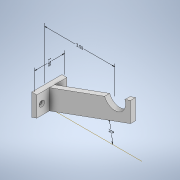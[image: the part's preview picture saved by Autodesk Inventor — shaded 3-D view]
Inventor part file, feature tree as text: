
AUTODESK INVENTOR PART (.ipt)
format: ipt  version: 2021.1 (Build 251245000, 245)  size: 155,136 bytes
history: native  units: in
note: dims shown in document units (in); Inventor stores cm internally (conversion verified against a paired STEP export)
features: other x4, sketch x4, extrude x3, hole x1
ambient origin geometry x8: Origin, YZ Plane, XZ Plane, XY Plane, X Axis, Y Axis, Z Axis, Center Point
bodies: Solid2 (feature_tree)
feature tree (12):
  other  "Annotations"
  extrude  "Extrusion3"  Depth=0.25in
  extrude  "Extrusion4"  Depth=1.5in
  sketch  "Sketch7"  dims[d26=1.075in d29=0.25in]
  extrude  "Extrusion5"  Depth=0.25in
  hole  "Hole3"  [1 undecoded]
  sketch  "Sketch5"  dims[d21=1.0in d22=0.25in]
  sketch  "Sketch6"  dims[d23=1.5in d24=0.0in d25=0.1374in]
  sketch  "Sketch8"  dims[d30=3.5in d31=0.25in d32=0.0in d33=0.0in d34=0.25in d35=0.25in d47=1.5in d48=0.0in d49=0.15in d50=0.75in d51=0.279in d52=0.25in d53=0.5635in d54=1.0in d55=0.8108in d56=0.2085in d57=0.331in d58=1.5in d59=2.3174in d60=0.1374in d62=3.5in]
  other  "Linear Dimension 1"
  other  "Angular Dimension 1"
  other  "Linear Dimension 3"
note: 1 required parameter value undecoded (feature->parameter linkage not recoverable at this tier; creation-order binding heuristic only, values carry confidence <= 0.55)
